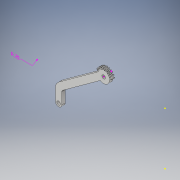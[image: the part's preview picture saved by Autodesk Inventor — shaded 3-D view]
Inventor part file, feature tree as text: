
AUTODESK INVENTOR PART (.ipt)
format: ipt  version: 2018 (Build 220112000, 112)  size: 211,968 bytes
history: native  units: in
note: dims shown in document units (in); Inventor stores cm internally (conversion verified against a paired STEP export)
features: sketch x8, extrude x4, other x2, plane x1, pattern_circular x1
ambient origin geometry x8: Origin, YZ Plane, XZ Plane, XY Plane, X Axis, Y Axis, Z Axis, Center Point
bodies: Solid1 (feature_tree)
feature tree (16):
  other  "Annotations"
  extrude  "Extrusion1"  Depth=0.1181in
  extrude  "Extrusion11"  Depth=0.1969in
  sketch  "Sketch15"  dims[d65=0.1969in d69=0.1094in]
  sketch  "Sketch16"  dims[d72=0.1969in d73=0.0in d82=0.066in]
  plane  "Work Plane2"
  sketch  "Sketch18"  dims[d83=0.0197in]
  extrude  "Extrusion13"  Depth=0.1094in
  sketch  "Sketch20"  dims[d85=0.0394in]
  extrude  "Extrusion15"  Depth=0.1969in
  pattern_circular  "Circular Pattern2"  [2 undecoded]
  sketch  "Sketch1"  dims[d7=0.1181in d8=0.0in d15=1.0in]
  sketch  "Sketch12"  dims[d47=0.1969in d48=0.1969in d63=2.1654in d64=0.1969in]
  sketch  "Sketch19"  dims[d84=0.0098in]
  sketch  "Sketch21"  dims[d86=0.0029in d87=0.1181in d88=0.0in d94=0.1181in d95=0.1181in d96=0.0in d97=3.937in d98=-0.9757in d105=0.1181in d28=1.2193in d29=0.25in]
  other  "Radial Dimension 1"
note: 2 required parameter values undecoded (feature->parameter linkage not recoverable at this tier; creation-order binding heuristic only, values carry confidence <= 0.55)
